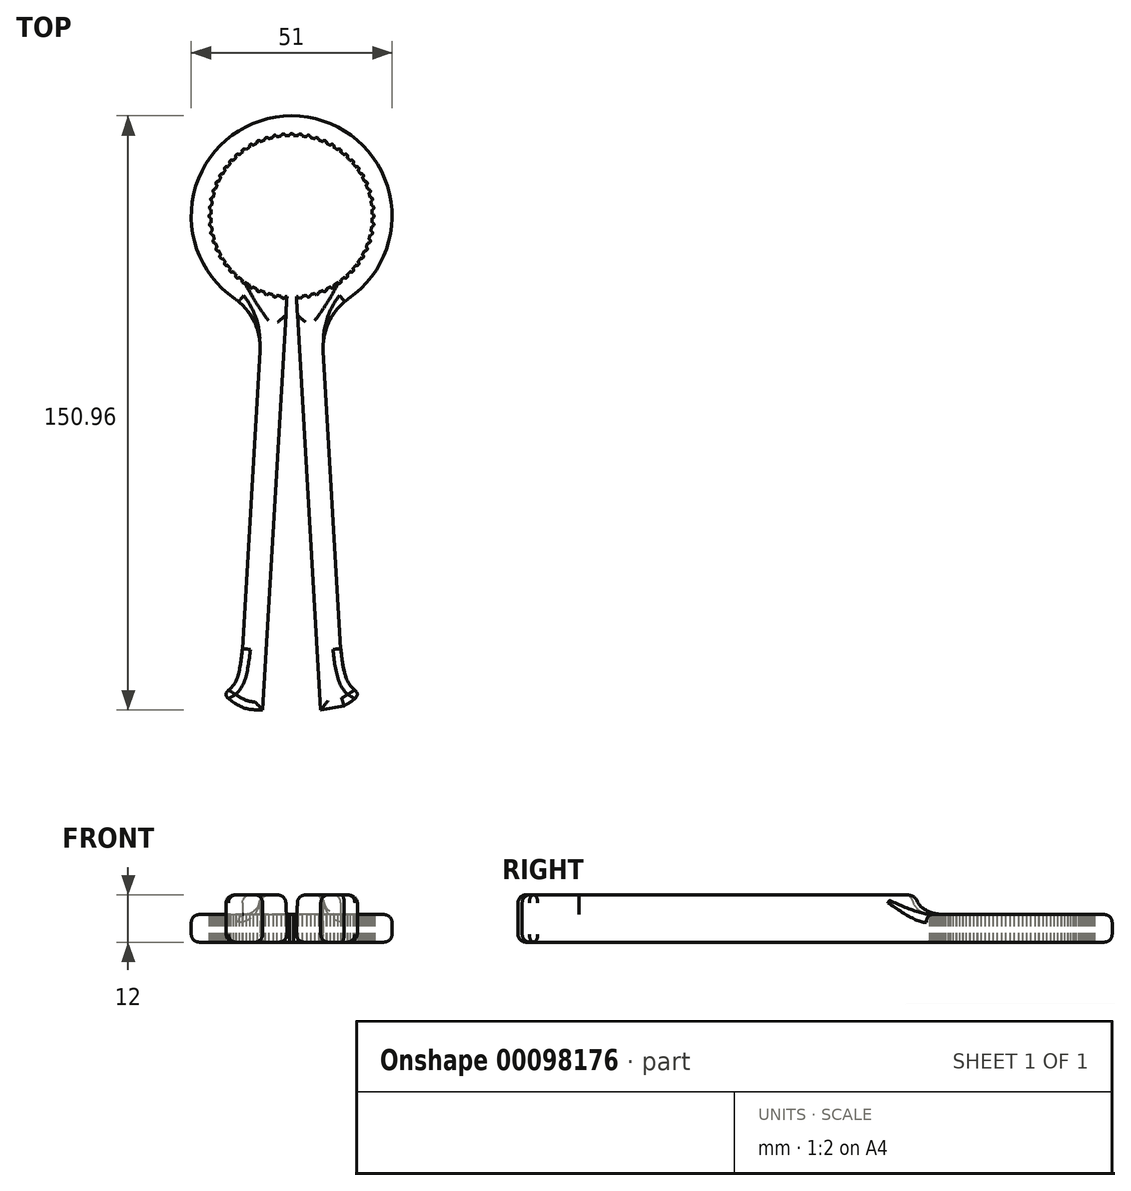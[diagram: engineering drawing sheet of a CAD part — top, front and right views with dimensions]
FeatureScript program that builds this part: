
annotation { "Feature Type Name" : "Feature", "Feature Type Description" : "" }
export const myFeature = defineFeature(function(context is Context, id is Id, definition is map)
    precondition{}
    {
        {
            var Q0;
            Q0=qCreatedBy(makeId("Top.planeOp"),FACE);
            var sketch = newSketch(context, id + "F0", { "sketchPlane" : qUnion([Q0])});
            skArc(sketch, "E0", {"start": v(-0.5, 20.5) * mm, "mid": v(0, 20) * mm, "end": v(0.5, 20.5) * mm, "construction": true});
            skArc(sketch, "E1", {"start": v(0.5, 20.5) * mm, "mid": v(0, 21) * mm, "end": v(-0.5, 20.5) * mm});
            skArc(sketch, "E2", {"start": v(-0.5, 20.5) * mm, "mid": v(-20.5, 0.35) * mm, "end": v(-1.2, -20.46) * mm});
            skArc(sketch, "E3", {"start": v(0.5, 20.5) * mm, "mid": v(0, 20.5) * mm, "end": v(-0.5, 20.5) * mm, "construction": true});
            skArc(sketch, "E4.1.0", {"start": v(-1.64, 20.43) * mm, "mid": v(-2.2, 20.88) * mm, "end": v(-2.64, 20.33) * mm});
            skArc(sketch, "E4.2.0", {"start": v(-3.77, 20.15) * mm, "mid": v(-4.37, 20.54) * mm, "end": v(-4.75, 19.94) * mm});
            skArc(sketch, "E4.3.0", {"start": v(-5.86, 19.65) * mm, "mid": v(-6.49, 19.97) * mm, "end": v(-6.8, 19.34) * mm});
            skArc(sketch, "E4.4.0", {"start": v(-7.88, 18.93) * mm, "mid": v(-8.54, 19.18) * mm, "end": v(-8.8, 18.52) * mm});
            skArc(sketch, "E4.5.0", {"start": v(-9.81, 18) * mm, "mid": v(-10.5, 18.19) * mm, "end": v(-10.68, 17.5) * mm});
            skArc(sketch, "E4.6.0", {"start": v(-11.64, 16.87) * mm, "mid": v(-12.34, 16.99) * mm, "end": v(-12.45, 16.29) * mm});
            skArc(sketch, "E4.7.0", {"start": v(-13.34, 15.56) * mm, "mid": v(-14.05, 15.6) * mm, "end": v(-14.08, 14.9) * mm});
            skArc(sketch, "E4.8.0", {"start": v(-14.9, 14.08) * mm, "mid": v(-15.6, 14.05) * mm, "end": v(-15.56, 13.34) * mm});
            skArc(sketch, "E4.9.0", {"start": v(-16.29, 12.45) * mm, "mid": v(-16.99, 12.34) * mm, "end": v(-16.87, 11.64) * mm});
            skArc(sketch, "E4.10.0", {"start": v(-17.5, 10.68) * mm, "mid": v(-18.19, 10.5) * mm, "end": v(-18, 9.81) * mm});
            skArc(sketch, "E4.11.0", {"start": v(-18.52, 8.8) * mm, "mid": v(-19.18, 8.54) * mm, "end": v(-18.93, 7.88) * mm});
            skArc(sketch, "E4.12.0", {"start": v(-19.34, 6.8) * mm, "mid": v(-19.97, 6.49) * mm, "end": v(-19.65, 5.86) * mm});
            skArc(sketch, "E4.13.0", {"start": v(-19.94, 4.75) * mm, "mid": v(-20.54, 4.37) * mm, "end": v(-20.15, 3.77) * mm});
            skArc(sketch, "E4.14.0", {"start": v(-20.33, 2.64) * mm, "mid": v(-20.88, 2.2) * mm, "end": v(-20.43, 1.64) * mm});
            skArc(sketch, "E4.15.0", {"start": v(-20.5, 0.5) * mm, "mid": v(-21, 0) * mm, "end": v(-20.5, -0.5) * mm});
            skArc(sketch, "E4.16.0", {"start": v(-20.43, -1.64) * mm, "mid": v(-20.88, -2.2) * mm, "end": v(-20.33, -2.64) * mm});
            skArc(sketch, "E4.17.0", {"start": v(-20.15, -3.77) * mm, "mid": v(-20.54, -4.37) * mm, "end": v(-19.94, -4.75) * mm});
            skArc(sketch, "E4.18.0", {"start": v(-19.65, -5.86) * mm, "mid": v(-19.97, -6.49) * mm, "end": v(-19.34, -6.8) * mm});
            skArc(sketch, "E4.19.0", {"start": v(-18.93, -7.88) * mm, "mid": v(-19.18, -8.54) * mm, "end": v(-18.52, -8.8) * mm});
            skArc(sketch, "E4.20.0", {"start": v(-18, -9.81) * mm, "mid": v(-18.19, -10.5) * mm, "end": v(-17.5, -10.68) * mm});
            skArc(sketch, "E4.21.0", {"start": v(-16.87, -11.64) * mm, "mid": v(-16.99, -12.34) * mm, "end": v(-16.29, -12.45) * mm});
            skArc(sketch, "E4.22.0", {"start": v(-15.56, -13.34) * mm, "mid": v(-15.6, -14.05) * mm, "end": v(-14.9, -14.08) * mm});
            skArc(sketch, "E4.23.0", {"start": v(-14.08, -14.9) * mm, "mid": v(-14.05, -15.6) * mm, "end": v(-13.34, -15.56) * mm});
            skArc(sketch, "E4.24.0", {"start": v(-12.45, -16.29) * mm, "mid": v(-12.34, -16.99) * mm, "end": v(-11.64, -16.87) * mm});
            skArc(sketch, "E4.25.0", {"start": v(-10.68, -17.5) * mm, "mid": v(-10.5, -18.19) * mm, "end": v(-9.81, -18) * mm});
            skArc(sketch, "E4.26.0", {"start": v(-8.8, -18.52) * mm, "mid": v(-8.54, -19.18) * mm, "end": v(-7.88, -18.93) * mm});
            skArc(sketch, "E4.27.0", {"start": v(-6.8, -19.34) * mm, "mid": v(-6.49, -19.97) * mm, "end": v(-5.86, -19.65) * mm});
            skArc(sketch, "E4.28.0", {"start": v(-4.75, -19.94) * mm, "mid": v(-4.37, -20.54) * mm, "end": v(-3.77, -20.15) * mm});
            skArc(sketch, "E4.29.0", {"start": v(-2.64, -20.33) * mm, "mid": v(-2.2, -20.88) * mm, "end": v(-1.64, -20.43) * mm});
            skArc(sketch, "E4.31.0", {"start": v(1.64, -20.43) * mm, "mid": v(2.2, -20.88) * mm, "end": v(2.64, -20.33) * mm});
            skArc(sketch, "E4.32.0", {"start": v(3.77, -20.15) * mm, "mid": v(4.37, -20.54) * mm, "end": v(4.75, -19.94) * mm});
            skArc(sketch, "E4.33.0", {"start": v(5.86, -19.65) * mm, "mid": v(6.49, -19.97) * mm, "end": v(6.8, -19.34) * mm});
            skArc(sketch, "E4.34.0", {"start": v(7.88, -18.93) * mm, "mid": v(8.54, -19.18) * mm, "end": v(8.8, -18.52) * mm});
            skArc(sketch, "E4.35.0", {"start": v(9.81, -18) * mm, "mid": v(10.5, -18.19) * mm, "end": v(10.68, -17.5) * mm});
            skArc(sketch, "E4.36.0", {"start": v(11.64, -16.87) * mm, "mid": v(12.34, -16.99) * mm, "end": v(12.45, -16.29) * mm});
            skArc(sketch, "E4.37.0", {"start": v(13.34, -15.56) * mm, "mid": v(14.05, -15.6) * mm, "end": v(14.08, -14.9) * mm});
            skArc(sketch, "E4.38.0", {"start": v(14.9, -14.08) * mm, "mid": v(15.6, -14.05) * mm, "end": v(15.56, -13.34) * mm});
            skArc(sketch, "E4.39.0", {"start": v(16.29, -12.45) * mm, "mid": v(16.99, -12.34) * mm, "end": v(16.87, -11.64) * mm});
            skArc(sketch, "E4.40.0", {"start": v(17.5, -10.68) * mm, "mid": v(18.19, -10.5) * mm, "end": v(18, -9.81) * mm});
            skArc(sketch, "E4.41.0", {"start": v(18.52, -8.8) * mm, "mid": v(19.18, -8.54) * mm, "end": v(18.93, -7.88) * mm});
            skArc(sketch, "E4.42.0", {"start": v(19.34, -6.8) * mm, "mid": v(19.97, -6.49) * mm, "end": v(19.65, -5.86) * mm});
            skArc(sketch, "E4.43.0", {"start": v(19.94, -4.75) * mm, "mid": v(20.54, -4.37) * mm, "end": v(20.15, -3.77) * mm});
            skArc(sketch, "E4.44.0", {"start": v(20.33, -2.64) * mm, "mid": v(20.88, -2.2) * mm, "end": v(20.43, -1.64) * mm});
            skArc(sketch, "E4.45.0", {"start": v(20.5, -0.5) * mm, "mid": v(21, 0) * mm, "end": v(20.5, 0.5) * mm});
            skArc(sketch, "E4.46.0", {"start": v(20.43, 1.64) * mm, "mid": v(20.88, 2.2) * mm, "end": v(20.33, 2.64) * mm});
            skArc(sketch, "E4.47.0", {"start": v(20.15, 3.77) * mm, "mid": v(20.54, 4.37) * mm, "end": v(19.94, 4.75) * mm});
            skArc(sketch, "E4.48.0", {"start": v(19.65, 5.86) * mm, "mid": v(19.97, 6.49) * mm, "end": v(19.34, 6.8) * mm});
            skArc(sketch, "E4.49.0", {"start": v(18.93, 7.88) * mm, "mid": v(19.18, 8.54) * mm, "end": v(18.52, 8.8) * mm});
            skArc(sketch, "E4.50.0", {"start": v(18, 9.81) * mm, "mid": v(18.19, 10.5) * mm, "end": v(17.5, 10.68) * mm});
            skArc(sketch, "E4.51.0", {"start": v(16.87, 11.64) * mm, "mid": v(16.99, 12.34) * mm, "end": v(16.29, 12.45) * mm});
            skArc(sketch, "E4.52.0", {"start": v(15.56, 13.34) * mm, "mid": v(15.6, 14.05) * mm, "end": v(14.9, 14.08) * mm});
            skArc(sketch, "E4.53.0", {"start": v(14.08, 14.9) * mm, "mid": v(14.05, 15.6) * mm, "end": v(13.34, 15.56) * mm});
            skArc(sketch, "E4.54.0", {"start": v(12.45, 16.29) * mm, "mid": v(12.34, 16.99) * mm, "end": v(11.64, 16.87) * mm});
            skArc(sketch, "E4.55.0", {"start": v(10.68, 17.5) * mm, "mid": v(10.5, 18.19) * mm, "end": v(9.81, 18) * mm});
            skArc(sketch, "E4.56.0", {"start": v(8.8, 18.52) * mm, "mid": v(8.54, 19.18) * mm, "end": v(7.88, 18.93) * mm});
            skArc(sketch, "E4.57.0", {"start": v(6.8, 19.34) * mm, "mid": v(6.49, 19.97) * mm, "end": v(5.86, 19.65) * mm});
            skArc(sketch, "E4.58.0", {"start": v(4.75, 19.94) * mm, "mid": v(4.37, 20.54) * mm, "end": v(3.77, 20.15) * mm});
            skArc(sketch, "E4.59.0", {"start": v(2.64, 20.33) * mm, "mid": v(2.2, 20.88) * mm, "end": v(1.64, 20.43) * mm});
            skLineSegment(sketch, "E5", {"start": v(0, 0) * mm, "end": v(0, -25.5) * mm, "construction": true});
            skLineSegment(sketch, "E6", {"start": v(0, 0) * mm, "end": v(-1.2, -20.46) * mm, "construction": true});
            skLineSegment(sketch, "E7.MirrorCS", {"start": v(0, 0) * mm, "end": v(1.2, -20.46) * mm, "construction": true});
            skLineSegment(sketch, "E8", {"start": v(-1.2, -20.46) * mm, "end": v(-7.4, -125.46) * mm});
            skArc(sketch, "E9", {"start": v(1.2, -20.46) * mm, "mid": v(20.5, 0.35) * mm, "end": v(0.5, 20.5) * mm});
            skLineSegment(sketch, "E10", {"start": v(1.2, -20.46) * mm, "end": v(1.5, -25.46) * mm});
            skArc(sketch, "E11", {"start": v(-1.5, -25.46) * mm, "mid": v(0, -25.5) * mm, "end": v(1.5, -25.46) * mm, "construction": true});
            skArc(sketch, "E12", {"start": v(1.5, -25.46) * mm, "mid": v(0, 25.5) * mm, "end": v(-1.5, -25.46) * mm});
            skPoint(sketch, "E13.orphan", {"position": v(-1.5, -25.46) * mm});
            skLineSegment(sketch, "E14", {"start": v(-7.45, -24.39) * mm, "end": v(-12.49, -109.92) * mm});
            skLineSegment(sketch, "E15.MirrorCS", {"start": v(1.2, -20.46) * mm, "end": v(7.4, -125.46) * mm});
            skLineSegment(sketch, "E16.MirrorCS", {"start": v(7.45, -24.39) * mm, "end": v(12.49, -109.92) * mm});
            skLineSegment(sketch, "E17.MirrorCS", {"start": v(13.34, -124.39) * mm, "end": v(7.4, -125.46) * mm});
            skLineSegment(sketch, "E18", {"start": v(0, 0) * mm, "end": v(0, -128.97) * mm, "construction": true});
            skFitSpline(sketch, "E19", {"points": [v(-12.49, -109.92) * mm, v(-14.7, -119.04) * mm, v(-16.69, -121.57) * mm, v(-13.34, -124.39) * mm, v(-7.4, -125.46) * mm], "startDerivative": vector(-3.66, -30.82) * mm, "endDerivative": vector(39.2, 0) * mm});
            skLineSegment(sketch, "E20", {"start": v(-12.49, -109.92) * mm, "end": v(-13.34, -124.39) * mm, "construction": true});
            skFitSpline(sketch, "E21.MirrorCS", {"points": [v(12.49, -109.92) * mm, v(14.7, -119.04) * mm, v(16.69, -121.57) * mm, v(13.34, -124.39) * mm, v(7.4, -125.46) * mm], "startDerivative": vector(3.66, -30.82) * mm, "endDerivative": vector(-39.2, 0) * mm});
            skLineSegment(sketch, "E22", {"start": v(12.49, -109.92) * mm, "end": v(13.34, -124.39) * mm, "construction": true});
            skSolve(sketch);
        }
        {
            var Q0;
            {var subQ63=sQuery(id+"F0.wireOp",EDGE,"E1");Q0=makeQuery(id+"F0.imprint","IMPRINT",FACE,{"disambiguationData":[TD([[makeQuery(id+"F0.imprint","IMPRINT",EDGE,{"derivedFrom":subQ63}),-1.0]])]});}
            var Q1;
            {var subQ4=sQuery(id+"F0.wireOp",EDGE,"E14");Q1=makeQuery(id+"F0.imprint","IMPRINT",FACE,{"disambiguationData":[TD([[makeQuery(id+"F0.imprint","IMPRINT",EDGE,{"derivedFrom":subQ4}),1.0]])]});}
            var Q2;
            {var subQ3=sQuery(id+"F0.wireOp",EDGE,"E16.MirrorCS");Q2=makeQuery(id+"F0.imprint","IMPRINT",FACE,{"disambiguationData":[TD([[makeQuery(id+"F0.imprint","IMPRINT",EDGE,{"derivedFrom":subQ3}),-1.0]])]});}
            extrude(context, id + "F1", {"entities" : qUnion([Q0, Q1, Q2]), "depth" : 7 * mm});
        }
        {
            var Q0;
            Q0=makeQuery(id+"F1.opExtrude","SWEPT_EDGE",EDGE,{"disambiguationData":[OSD([sQuery(id+"F0.wireOp",EDGE,"E12"),sQuery(id+"F0.wireOp",EDGE,"E14")])]});
            var Q1;
            Q1=makeQuery(id+"F1.opExtrude","SWEPT_EDGE",EDGE,{"disambiguationData":[OSD([sQuery(id+"F0.wireOp",EDGE,"E12"),sQuery(id+"F0.wireOp",EDGE,"E16.MirrorCS")])]});
            fillet(context, id + "F2", {"entities" : qUnion([Q0, Q1]), "radius" : 15 * mm, "tangentPropagation" : true, "allowEdgeOverflow" : false});
        }
        {
            var Q0;
            Q0=makeQuery(id+"F1.opExtrude","SWEPT_EDGE",EDGE,{"disambiguationData":[OSD([sQuery(id+"F0.wireOp",EDGE,"E14"),sQuery(id+"F0.wireOp",EDGE,"XZCalI78-Oa4T-IdOj-XRzA-xECI0NogZIKb")])]});
            var Q1;
            Q1=makeQuery(id+"F1.opExtrude","SWEPT_EDGE",EDGE,{"disambiguationData":[OSD([sQuery(id+"F0.wireOp",EDGE,"E16.MirrorCS"),sQuery(id+"F0.wireOp",EDGE,"E17.MirrorCS")])]});
            fillet(context, id + "F3", {"entities" : qUnion([Q0, Q1]), "radius" : 5 * mm, "tangentPropagation" : true, "allowEdgeOverflow" : false});
        }
        {
            var Q0;
            {var subQ4=sQuery(id+"F0.wireOp",EDGE,"E14");Q0=makeQuery(id+"F0.imprint","IMPRINT",FACE,{"disambiguationData":[TD([[makeQuery(id+"F0.imprint","IMPRINT",EDGE,{"derivedFrom":subQ4}),1.0]])]});}
            var Q1;
            {var subQ3=sQuery(id+"F0.wireOp",EDGE,"E16.MirrorCS");Q1=makeQuery(id+"F0.imprint","IMPRINT",FACE,{"disambiguationData":[TD([[makeQuery(id+"F0.imprint","IMPRINT",EDGE,{"derivedFrom":subQ3}),-1.0]])]});}
            extrude(context, id + "F4", {"entities" : qUnion([Q0, Q1]), "operationType" : NewBodyOperationType.ADD, "depth" : 12 * mm});
        }
        {
            var Q0;
            {var subQ0=sQuery(id+"F0.wireOp",EDGE,"E14");Q0=makeQuery(id+"F4.boolean.opBoolean","INTERSECT",EDGE,{"derivedFrom":[makeQuery(id+"F1.opExtrude","CAP_FACE",FACE,{"disambiguationData":[OSD([sQuery(id+"F0.wireOp",EDGE,"E1"),sQuery(id+"F0.wireOp",EDGE,"E2"),sQuery(id+"F0.wireOp",EDGE,"E4.1.0"),sQuery(id+"F0.wireOp",EDGE,"E4.2.0"),sQuery(id+"F0.wireOp",EDGE,"E4.3.0"),sQuery(id+"F0.wireOp",EDGE,"E4.4.0"),sQuery(id+"F0.wireOp",EDGE,"E4.5.0"),sQuery(id+"F0.wireOp",EDGE,"E4.6.0"),sQuery(id+"F0.wireOp",EDGE,"E4.7.0"),sQuery(id+"F0.wireOp",EDGE,"E4.8.0"),sQuery(id+"F0.wireOp",EDGE,"E4.9.0"),sQuery(id+"F0.wireOp",EDGE,"E4.10.0"),sQuery(id+"F0.wireOp",EDGE,"E4.11.0"),sQuery(id+"F0.wireOp",EDGE,"E4.12.0"),sQuery(id+"F0.wireOp",EDGE,"E4.13.0"),sQuery(id+"F0.wireOp",EDGE,"E4.14.0"),sQuery(id+"F0.wireOp",EDGE,"E4.15.0"),sQuery(id+"F0.wireOp",EDGE,"E4.16.0"),sQuery(id+"F0.wireOp",EDGE,"E4.17.0"),sQuery(id+"F0.wireOp",EDGE,"E4.18.0"),sQuery(id+"F0.wireOp",EDGE,"E4.19.0"),sQuery(id+"F0.wireOp",EDGE,"E4.20.0"),sQuery(id+"F0.wireOp",EDGE,"E4.21.0"),sQuery(id+"F0.wireOp",EDGE,"E4.22.0"),sQuery(id+"F0.wireOp",EDGE,"E4.23.0"),sQuery(id+"F0.wireOp",EDGE,"E4.24.0"),sQuery(id+"F0.wireOp",EDGE,"E4.25.0"),sQuery(id+"F0.wireOp",EDGE,"E4.26.0"),sQuery(id+"F0.wireOp",EDGE,"E4.27.0"),sQuery(id+"F0.wireOp",EDGE,"E4.28.0"),sQuery(id+"F0.wireOp",EDGE,"E4.29.0"),sQuery(id+"F0.wireOp",EDGE,"E4.31.0"),sQuery(id+"F0.wireOp",EDGE,"E4.32.0"),sQuery(id+"F0.wireOp",EDGE,"E4.33.0"),sQuery(id+"F0.wireOp",EDGE,"E4.34.0"),sQuery(id+"F0.wireOp",EDGE,"E4.35.0"),sQuery(id+"F0.wireOp",EDGE,"E4.36.0"),sQuery(id+"F0.wireOp",EDGE,"E4.37.0"),sQuery(id+"F0.wireOp",EDGE,"E4.38.0"),sQuery(id+"F0.wireOp",EDGE,"E4.39.0"),sQuery(id+"F0.wireOp",EDGE,"E4.40.0"),sQuery(id+"F0.wireOp",EDGE,"E4.41.0"),sQuery(id+"F0.wireOp",EDGE,"E4.42.0"),sQuery(id+"F0.wireOp",EDGE,"E4.43.0"),sQuery(id+"F0.wireOp",EDGE,"E4.44.0"),sQuery(id+"F0.wireOp",EDGE,"E4.45.0"),sQuery(id+"F0.wireOp",EDGE,"E4.46.0"),sQuery(id+"F0.wireOp",EDGE,"E4.47.0"),sQuery(id+"F0.wireOp",EDGE,"E4.48.0"),sQuery(id+"F0.wireOp",EDGE,"E4.49.0"),sQuery(id+"F0.wireOp",EDGE,"E4.50.0"),sQuery(id+"F0.wireOp",EDGE,"E4.51.0"),sQuery(id+"F0.wireOp",EDGE,"E4.52.0"),sQuery(id+"F0.wireOp",EDGE,"E4.53.0"),sQuery(id+"F0.wireOp",EDGE,"E4.54.0"),sQuery(id+"F0.wireOp",EDGE,"E4.55.0"),sQuery(id+"F0.wireOp",EDGE,"E4.56.0"),sQuery(id+"F0.wireOp",EDGE,"E4.57.0"),sQuery(id+"F0.wireOp",EDGE,"E4.58.0"),sQuery(id+"F0.wireOp",EDGE,"E4.59.0"),sQuery(id+"F0.wireOp",EDGE,"E8"),sQuery(id+"F0.wireOp",EDGE,"E9"),sQuery(id+"F0.wireOp",EDGE,"E12"),subQ0,sQuery(id+"F0.wireOp",EDGE,"E15.MirrorCS"),sQuery(id+"F0.wireOp",EDGE,"E16.MirrorCS"),sQuery(id+"F0.wireOp",EDGE,"E17.MirrorCS"),sQuery(id+"F0.wireOp",EDGE,"E19"),sQuery(id+"F0.wireOp",EDGE,"E21.MirrorCS")])],"isStart":false}),makeQuery(id+"F4.opExtrude","SWEPT_FACE",FACE,{"disambiguationData":[OSD([subQ0])]})]});}
            fillet(context, id + "F5", {"entities" : qUnion([Q0]), "radius" : 5 * mm, "tangentPropagation" : true, "allowEdgeOverflow" : false});
        }
        {
            var Q0;
            {var subQ0=sQuery(id+"F0.wireOp",EDGE,"E16.MirrorCS");Q0=makeQuery(id+"F4.boolean.opBoolean","INTERSECT",EDGE,{"derivedFrom":[makeQuery(id+"F1.opExtrude","CAP_FACE",FACE,{"disambiguationData":[OSD([sQuery(id+"F0.wireOp",EDGE,"E1"),sQuery(id+"F0.wireOp",EDGE,"E2"),sQuery(id+"F0.wireOp",EDGE,"E4.1.0"),sQuery(id+"F0.wireOp",EDGE,"E4.2.0"),sQuery(id+"F0.wireOp",EDGE,"E4.3.0"),sQuery(id+"F0.wireOp",EDGE,"E4.4.0"),sQuery(id+"F0.wireOp",EDGE,"E4.5.0"),sQuery(id+"F0.wireOp",EDGE,"E4.6.0"),sQuery(id+"F0.wireOp",EDGE,"E4.7.0"),sQuery(id+"F0.wireOp",EDGE,"E4.8.0"),sQuery(id+"F0.wireOp",EDGE,"E4.9.0"),sQuery(id+"F0.wireOp",EDGE,"E4.10.0"),sQuery(id+"F0.wireOp",EDGE,"E4.11.0"),sQuery(id+"F0.wireOp",EDGE,"E4.12.0"),sQuery(id+"F0.wireOp",EDGE,"E4.13.0"),sQuery(id+"F0.wireOp",EDGE,"E4.14.0"),sQuery(id+"F0.wireOp",EDGE,"E4.15.0"),sQuery(id+"F0.wireOp",EDGE,"E4.16.0"),sQuery(id+"F0.wireOp",EDGE,"E4.17.0"),sQuery(id+"F0.wireOp",EDGE,"E4.18.0"),sQuery(id+"F0.wireOp",EDGE,"E4.19.0"),sQuery(id+"F0.wireOp",EDGE,"E4.20.0"),sQuery(id+"F0.wireOp",EDGE,"E4.21.0"),sQuery(id+"F0.wireOp",EDGE,"E4.22.0"),sQuery(id+"F0.wireOp",EDGE,"E4.23.0"),sQuery(id+"F0.wireOp",EDGE,"E4.24.0"),sQuery(id+"F0.wireOp",EDGE,"E4.25.0"),sQuery(id+"F0.wireOp",EDGE,"E4.26.0"),sQuery(id+"F0.wireOp",EDGE,"E4.27.0"),sQuery(id+"F0.wireOp",EDGE,"E4.28.0"),sQuery(id+"F0.wireOp",EDGE,"E4.29.0"),sQuery(id+"F0.wireOp",EDGE,"E4.31.0"),sQuery(id+"F0.wireOp",EDGE,"E4.32.0"),sQuery(id+"F0.wireOp",EDGE,"E4.33.0"),sQuery(id+"F0.wireOp",EDGE,"E4.34.0"),sQuery(id+"F0.wireOp",EDGE,"E4.35.0"),sQuery(id+"F0.wireOp",EDGE,"E4.36.0"),sQuery(id+"F0.wireOp",EDGE,"E4.37.0"),sQuery(id+"F0.wireOp",EDGE,"E4.38.0"),sQuery(id+"F0.wireOp",EDGE,"E4.39.0"),sQuery(id+"F0.wireOp",EDGE,"E4.40.0"),sQuery(id+"F0.wireOp",EDGE,"E4.41.0"),sQuery(id+"F0.wireOp",EDGE,"E4.42.0"),sQuery(id+"F0.wireOp",EDGE,"E4.43.0"),sQuery(id+"F0.wireOp",EDGE,"E4.44.0"),sQuery(id+"F0.wireOp",EDGE,"E4.45.0"),sQuery(id+"F0.wireOp",EDGE,"E4.46.0"),sQuery(id+"F0.wireOp",EDGE,"E4.47.0"),sQuery(id+"F0.wireOp",EDGE,"E4.48.0"),sQuery(id+"F0.wireOp",EDGE,"E4.49.0"),sQuery(id+"F0.wireOp",EDGE,"E4.50.0"),sQuery(id+"F0.wireOp",EDGE,"E4.51.0"),sQuery(id+"F0.wireOp",EDGE,"E4.52.0"),sQuery(id+"F0.wireOp",EDGE,"E4.53.0"),sQuery(id+"F0.wireOp",EDGE,"E4.54.0"),sQuery(id+"F0.wireOp",EDGE,"E4.55.0"),sQuery(id+"F0.wireOp",EDGE,"E4.56.0"),sQuery(id+"F0.wireOp",EDGE,"E4.57.0"),sQuery(id+"F0.wireOp",EDGE,"E4.58.0"),sQuery(id+"F0.wireOp",EDGE,"E4.59.0"),sQuery(id+"F0.wireOp",EDGE,"E8"),sQuery(id+"F0.wireOp",EDGE,"E9"),sQuery(id+"F0.wireOp",EDGE,"E12"),sQuery(id+"F0.wireOp",EDGE,"E14"),sQuery(id+"F0.wireOp",EDGE,"E15.MirrorCS"),subQ0,sQuery(id+"F0.wireOp",EDGE,"E17.MirrorCS"),sQuery(id+"F0.wireOp",EDGE,"E19"),sQuery(id+"F0.wireOp",EDGE,"E21.MirrorCS")])],"isStart":false}),makeQuery(id+"F4.opExtrude","SWEPT_FACE",FACE,{"disambiguationData":[OSD([subQ0])]})]});}
            fillet(context, id + "F6", {"entities" : qUnion([Q0]), "radius" : 5 * mm, "tangentPropagation" : true, "allowEdgeOverflow" : false});
        }
        {
            var Q0;
            {var subQ0=sQuery(id+"F0.wireOp",EDGE,"E15.MirrorCS");var subQ1=sQuery(id+"F0.wireOp",EDGE,"E12");var subQ2=sQuery(id+"F0.wireOp",EDGE,"E16.MirrorCS");Q0=makeQuery(id+"F4.boolean.opBoolean","INTERSECT",EDGE,{"derivedFrom":[makeQuery(id+"F1.opExtrude","CAP_FACE",FACE,{"disambiguationData":[OSD([sQuery(id+"F0.wireOp",EDGE,"E1"),sQuery(id+"F0.wireOp",EDGE,"E2"),sQuery(id+"F0.wireOp",EDGE,"E4.1.0"),sQuery(id+"F0.wireOp",EDGE,"E4.2.0"),sQuery(id+"F0.wireOp",EDGE,"E4.3.0"),sQuery(id+"F0.wireOp",EDGE,"E4.4.0"),sQuery(id+"F0.wireOp",EDGE,"E4.5.0"),sQuery(id+"F0.wireOp",EDGE,"E4.6.0"),sQuery(id+"F0.wireOp",EDGE,"E4.7.0"),sQuery(id+"F0.wireOp",EDGE,"E4.8.0"),sQuery(id+"F0.wireOp",EDGE,"E4.9.0"),sQuery(id+"F0.wireOp",EDGE,"E4.10.0"),sQuery(id+"F0.wireOp",EDGE,"E4.11.0"),sQuery(id+"F0.wireOp",EDGE,"E4.12.0"),sQuery(id+"F0.wireOp",EDGE,"E4.13.0"),sQuery(id+"F0.wireOp",EDGE,"E4.14.0"),sQuery(id+"F0.wireOp",EDGE,"E4.15.0"),sQuery(id+"F0.wireOp",EDGE,"E4.16.0"),sQuery(id+"F0.wireOp",EDGE,"E4.17.0"),sQuery(id+"F0.wireOp",EDGE,"E4.18.0"),sQuery(id+"F0.wireOp",EDGE,"E4.19.0"),sQuery(id+"F0.wireOp",EDGE,"E4.20.0"),sQuery(id+"F0.wireOp",EDGE,"E4.21.0"),sQuery(id+"F0.wireOp",EDGE,"E4.22.0"),sQuery(id+"F0.wireOp",EDGE,"E4.23.0"),sQuery(id+"F0.wireOp",EDGE,"E4.24.0"),sQuery(id+"F0.wireOp",EDGE,"E4.25.0"),sQuery(id+"F0.wireOp",EDGE,"E4.26.0"),sQuery(id+"F0.wireOp",EDGE,"E4.27.0"),sQuery(id+"F0.wireOp",EDGE,"E4.28.0"),sQuery(id+"F0.wireOp",EDGE,"E4.29.0"),sQuery(id+"F0.wireOp",EDGE,"E4.31.0"),sQuery(id+"F0.wireOp",EDGE,"E4.32.0"),sQuery(id+"F0.wireOp",EDGE,"E4.33.0"),sQuery(id+"F0.wireOp",EDGE,"E4.34.0"),sQuery(id+"F0.wireOp",EDGE,"E4.35.0"),sQuery(id+"F0.wireOp",EDGE,"E4.36.0"),sQuery(id+"F0.wireOp",EDGE,"E4.37.0"),sQuery(id+"F0.wireOp",EDGE,"E4.38.0"),sQuery(id+"F0.wireOp",EDGE,"E4.39.0"),sQuery(id+"F0.wireOp",EDGE,"E4.40.0"),sQuery(id+"F0.wireOp",EDGE,"E4.41.0"),sQuery(id+"F0.wireOp",EDGE,"E4.42.0"),sQuery(id+"F0.wireOp",EDGE,"E4.43.0"),sQuery(id+"F0.wireOp",EDGE,"E4.44.0"),sQuery(id+"F0.wireOp",EDGE,"E4.45.0"),sQuery(id+"F0.wireOp",EDGE,"E4.46.0"),sQuery(id+"F0.wireOp",EDGE,"E4.47.0"),sQuery(id+"F0.wireOp",EDGE,"E4.48.0"),sQuery(id+"F0.wireOp",EDGE,"E4.49.0"),sQuery(id+"F0.wireOp",EDGE,"E4.50.0"),sQuery(id+"F0.wireOp",EDGE,"E4.51.0"),sQuery(id+"F0.wireOp",EDGE,"E4.52.0"),sQuery(id+"F0.wireOp",EDGE,"E4.53.0"),sQuery(id+"F0.wireOp",EDGE,"E4.54.0"),sQuery(id+"F0.wireOp",EDGE,"E4.55.0"),sQuery(id+"F0.wireOp",EDGE,"E4.56.0"),sQuery(id+"F0.wireOp",EDGE,"E4.57.0"),sQuery(id+"F0.wireOp",EDGE,"E4.58.0"),sQuery(id+"F0.wireOp",EDGE,"E4.59.0"),sQuery(id+"F0.wireOp",EDGE,"E8"),sQuery(id+"F0.wireOp",EDGE,"E9"),subQ1,sQuery(id+"F0.wireOp",EDGE,"E14"),subQ0,subQ2,sQuery(id+"F0.wireOp",EDGE,"E17.MirrorCS"),sQuery(id+"F0.wireOp",EDGE,"E19"),sQuery(id+"F0.wireOp",EDGE,"E21.MirrorCS")])],"isStart":false}),makeQuery(id+"F4.opExtrude","SWEPT_FACE",FACE,{"disambiguationData":[OSD([subQ1]),TDD([makeQuery(id+"F0.imprint","IMPRINT",EDGE,{"disambiguationData":[TD([[makeQuery(id+"F0.imprint","INTERSECT",VERTEX,{"derivedFrom":[subQ1,subQ0]}),-1.0]])],"derivedFrom":subQ1})])]})]});}
            var Q1;
            {var subQ0=sQuery(id+"F0.wireOp",EDGE,"E12");var subQ1=sQuery(id+"F0.wireOp",EDGE,"E8");var subQ2=sQuery(id+"F0.wireOp",EDGE,"E14");Q1=makeQuery(id+"F4.boolean.opBoolean","INTERSECT",EDGE,{"derivedFrom":[makeQuery(id+"F1.opExtrude","CAP_FACE",FACE,{"disambiguationData":[OSD([sQuery(id+"F0.wireOp",EDGE,"E1"),sQuery(id+"F0.wireOp",EDGE,"E2"),sQuery(id+"F0.wireOp",EDGE,"E4.1.0"),sQuery(id+"F0.wireOp",EDGE,"E4.2.0"),sQuery(id+"F0.wireOp",EDGE,"E4.3.0"),sQuery(id+"F0.wireOp",EDGE,"E4.4.0"),sQuery(id+"F0.wireOp",EDGE,"E4.5.0"),sQuery(id+"F0.wireOp",EDGE,"E4.6.0"),sQuery(id+"F0.wireOp",EDGE,"E4.7.0"),sQuery(id+"F0.wireOp",EDGE,"E4.8.0"),sQuery(id+"F0.wireOp",EDGE,"E4.9.0"),sQuery(id+"F0.wireOp",EDGE,"E4.10.0"),sQuery(id+"F0.wireOp",EDGE,"E4.11.0"),sQuery(id+"F0.wireOp",EDGE,"E4.12.0"),sQuery(id+"F0.wireOp",EDGE,"E4.13.0"),sQuery(id+"F0.wireOp",EDGE,"E4.14.0"),sQuery(id+"F0.wireOp",EDGE,"E4.15.0"),sQuery(id+"F0.wireOp",EDGE,"E4.16.0"),sQuery(id+"F0.wireOp",EDGE,"E4.17.0"),sQuery(id+"F0.wireOp",EDGE,"E4.18.0"),sQuery(id+"F0.wireOp",EDGE,"E4.19.0"),sQuery(id+"F0.wireOp",EDGE,"E4.20.0"),sQuery(id+"F0.wireOp",EDGE,"E4.21.0"),sQuery(id+"F0.wireOp",EDGE,"E4.22.0"),sQuery(id+"F0.wireOp",EDGE,"E4.23.0"),sQuery(id+"F0.wireOp",EDGE,"E4.24.0"),sQuery(id+"F0.wireOp",EDGE,"E4.25.0"),sQuery(id+"F0.wireOp",EDGE,"E4.26.0"),sQuery(id+"F0.wireOp",EDGE,"E4.27.0"),sQuery(id+"F0.wireOp",EDGE,"E4.28.0"),sQuery(id+"F0.wireOp",EDGE,"E4.29.0"),sQuery(id+"F0.wireOp",EDGE,"E4.31.0"),sQuery(id+"F0.wireOp",EDGE,"E4.32.0"),sQuery(id+"F0.wireOp",EDGE,"E4.33.0"),sQuery(id+"F0.wireOp",EDGE,"E4.34.0"),sQuery(id+"F0.wireOp",EDGE,"E4.35.0"),sQuery(id+"F0.wireOp",EDGE,"E4.36.0"),sQuery(id+"F0.wireOp",EDGE,"E4.37.0"),sQuery(id+"F0.wireOp",EDGE,"E4.38.0"),sQuery(id+"F0.wireOp",EDGE,"E4.39.0"),sQuery(id+"F0.wireOp",EDGE,"E4.40.0"),sQuery(id+"F0.wireOp",EDGE,"E4.41.0"),sQuery(id+"F0.wireOp",EDGE,"E4.42.0"),sQuery(id+"F0.wireOp",EDGE,"E4.43.0"),sQuery(id+"F0.wireOp",EDGE,"E4.44.0"),sQuery(id+"F0.wireOp",EDGE,"E4.45.0"),sQuery(id+"F0.wireOp",EDGE,"E4.46.0"),sQuery(id+"F0.wireOp",EDGE,"E4.47.0"),sQuery(id+"F0.wireOp",EDGE,"E4.48.0"),sQuery(id+"F0.wireOp",EDGE,"E4.49.0"),sQuery(id+"F0.wireOp",EDGE,"E4.50.0"),sQuery(id+"F0.wireOp",EDGE,"E4.51.0"),sQuery(id+"F0.wireOp",EDGE,"E4.52.0"),sQuery(id+"F0.wireOp",EDGE,"E4.53.0"),sQuery(id+"F0.wireOp",EDGE,"E4.54.0"),sQuery(id+"F0.wireOp",EDGE,"E4.55.0"),sQuery(id+"F0.wireOp",EDGE,"E4.56.0"),sQuery(id+"F0.wireOp",EDGE,"E4.57.0"),sQuery(id+"F0.wireOp",EDGE,"E4.58.0"),sQuery(id+"F0.wireOp",EDGE,"E4.59.0"),subQ1,sQuery(id+"F0.wireOp",EDGE,"E9"),subQ0,subQ2,sQuery(id+"F0.wireOp",EDGE,"E15.MirrorCS"),sQuery(id+"F0.wireOp",EDGE,"E16.MirrorCS"),sQuery(id+"F0.wireOp",EDGE,"E17.MirrorCS"),sQuery(id+"F0.wireOp",EDGE,"E19"),sQuery(id+"F0.wireOp",EDGE,"E21.MirrorCS")])],"isStart":false}),makeQuery(id+"F4.opExtrude","SWEPT_FACE",FACE,{"disambiguationData":[OSD([subQ0]),TDD([makeQuery(id+"F0.imprint","IMPRINT",EDGE,{"disambiguationData":[TD([[makeQuery(id+"F0.imprint","INTERSECT",VERTEX,{"derivedFrom":[subQ1,subQ0]}),1.0]])],"derivedFrom":subQ0})])]})]});}
            fillet(context, id + "F7", {"entities" : qUnion([Q0, Q1]), "radius" : 5 * mm, "tangentPropagation" : true, "allowEdgeOverflow" : false});
        }
        {
            var Q0;
            Q0=makeQuery(id+"F4.opExtrude","CAP_EDGE",EDGE,{"disambiguationData":[OSD([sQuery(id+"F0.wireOp",EDGE,"E14")])],"isStart":false});
            var Q1;
            {var subQ0=sQuery(id+"F0.wireOp",EDGE,"E19");var subQ1=sQuery(id+"F0.wireOp",EDGE,"E14");var subQ2=sQuery(id+"F0.wireOp",EDGE,"E12");var subQ3=sQuery(id+"F0.wireOp",EDGE,"E8");Q1=makeQuery(id+"F7.opFillet","BLEND_EDGE",EDGE,{"blendedFrom":[makeQuery(id+"F4.boolean.opBoolean","INTERSECT",EDGE,{"derivedFrom":[makeQuery(id+"F1.opExtrude","CAP_FACE",FACE,{"disambiguationData":[OSD([sQuery(id+"F0.wireOp",EDGE,"E1"),sQuery(id+"F0.wireOp",EDGE,"E2"),sQuery(id+"F0.wireOp",EDGE,"E4.1.0"),sQuery(id+"F0.wireOp",EDGE,"E4.2.0"),sQuery(id+"F0.wireOp",EDGE,"E4.3.0"),sQuery(id+"F0.wireOp",EDGE,"E4.4.0"),sQuery(id+"F0.wireOp",EDGE,"E4.5.0"),sQuery(id+"F0.wireOp",EDGE,"E4.6.0"),sQuery(id+"F0.wireOp",EDGE,"E4.7.0"),sQuery(id+"F0.wireOp",EDGE,"E4.8.0"),sQuery(id+"F0.wireOp",EDGE,"E4.9.0"),sQuery(id+"F0.wireOp",EDGE,"E4.10.0"),sQuery(id+"F0.wireOp",EDGE,"E4.11.0"),sQuery(id+"F0.wireOp",EDGE,"E4.12.0"),sQuery(id+"F0.wireOp",EDGE,"E4.13.0"),sQuery(id+"F0.wireOp",EDGE,"E4.14.0"),sQuery(id+"F0.wireOp",EDGE,"E4.15.0"),sQuery(id+"F0.wireOp",EDGE,"E4.16.0"),sQuery(id+"F0.wireOp",EDGE,"E4.17.0"),sQuery(id+"F0.wireOp",EDGE,"E4.18.0"),sQuery(id+"F0.wireOp",EDGE,"E4.19.0"),sQuery(id+"F0.wireOp",EDGE,"E4.20.0"),sQuery(id+"F0.wireOp",EDGE,"E4.21.0"),sQuery(id+"F0.wireOp",EDGE,"E4.22.0"),sQuery(id+"F0.wireOp",EDGE,"E4.23.0"),sQuery(id+"F0.wireOp",EDGE,"E4.24.0"),sQuery(id+"F0.wireOp",EDGE,"E4.25.0"),sQuery(id+"F0.wireOp",EDGE,"E4.26.0"),sQuery(id+"F0.wireOp",EDGE,"E4.27.0"),sQuery(id+"F0.wireOp",EDGE,"E4.28.0"),sQuery(id+"F0.wireOp",EDGE,"E4.29.0"),sQuery(id+"F0.wireOp",EDGE,"E4.31.0"),sQuery(id+"F0.wireOp",EDGE,"E4.32.0"),sQuery(id+"F0.wireOp",EDGE,"E4.33.0"),sQuery(id+"F0.wireOp",EDGE,"E4.34.0"),sQuery(id+"F0.wireOp",EDGE,"E4.35.0"),sQuery(id+"F0.wireOp",EDGE,"E4.36.0"),sQuery(id+"F0.wireOp",EDGE,"E4.37.0"),sQuery(id+"F0.wireOp",EDGE,"E4.38.0"),sQuery(id+"F0.wireOp",EDGE,"E4.39.0"),sQuery(id+"F0.wireOp",EDGE,"E4.40.0"),sQuery(id+"F0.wireOp",EDGE,"E4.41.0"),sQuery(id+"F0.wireOp",EDGE,"E4.42.0"),sQuery(id+"F0.wireOp",EDGE,"E4.43.0"),sQuery(id+"F0.wireOp",EDGE,"E4.44.0"),sQuery(id+"F0.wireOp",EDGE,"E4.45.0"),sQuery(id+"F0.wireOp",EDGE,"E4.46.0"),sQuery(id+"F0.wireOp",EDGE,"E4.47.0"),sQuery(id+"F0.wireOp",EDGE,"E4.48.0"),sQuery(id+"F0.wireOp",EDGE,"E4.49.0"),sQuery(id+"F0.wireOp",EDGE,"E4.50.0"),sQuery(id+"F0.wireOp",EDGE,"E4.51.0"),sQuery(id+"F0.wireOp",EDGE,"E4.52.0"),sQuery(id+"F0.wireOp",EDGE,"E4.53.0"),sQuery(id+"F0.wireOp",EDGE,"E4.54.0"),sQuery(id+"F0.wireOp",EDGE,"E4.55.0"),sQuery(id+"F0.wireOp",EDGE,"E4.56.0"),sQuery(id+"F0.wireOp",EDGE,"E4.57.0"),sQuery(id+"F0.wireOp",EDGE,"E4.58.0"),sQuery(id+"F0.wireOp",EDGE,"E4.59.0"),subQ3,sQuery(id+"F0.wireOp",EDGE,"E9"),subQ2,subQ1,sQuery(id+"F0.wireOp",EDGE,"E15.MirrorCS"),sQuery(id+"F0.wireOp",EDGE,"E16.MirrorCS"),sQuery(id+"F0.wireOp",EDGE,"E17.MirrorCS"),subQ0,sQuery(id+"F0.wireOp",EDGE,"E21.MirrorCS")])],"isStart":false}),makeQuery(id+"F4.opExtrude","SWEPT_FACE",FACE,{"disambiguationData":[OSD([subQ2]),TDD([makeQuery(id+"F0.imprint","IMPRINT",EDGE,{"disambiguationData":[TD([[makeQuery(id+"F0.imprint","INTERSECT",VERTEX,{"derivedFrom":[subQ3,subQ2]}),1.0]])],"derivedFrom":subQ2})])]})]}),makeQuery(id+"F4.opExtrude","CAP_FACE",FACE,{"disambiguationData":[OSD([subQ3,subQ2,subQ1,subQ0])],"isStart":false})],"blendedInto":[makeQuery(id+"F4.opExtrude","CAP_FACE",FACE,{"disambiguationData":[OSD([subQ3,subQ2,subQ1,subQ0])],"isStart":false})]});}
            var Q2;
            {var subQ0=sQuery(id+"F0.wireOp",EDGE,"E19");var subQ1=sQuery(id+"F0.wireOp",EDGE,"E14");var subQ2=sQuery(id+"F0.wireOp",EDGE,"E12");var subQ3=sQuery(id+"F0.wireOp",EDGE,"E8");Q2=makeQuery(id+"F5.opFillet","BLEND_EDGE",EDGE,{"blendedFrom":[makeQuery(id+"F4.boolean.opBoolean","INTERSECT",EDGE,{"derivedFrom":[makeQuery(id+"F1.opExtrude","CAP_FACE",FACE,{"disambiguationData":[OSD([sQuery(id+"F0.wireOp",EDGE,"E1"),sQuery(id+"F0.wireOp",EDGE,"E2"),sQuery(id+"F0.wireOp",EDGE,"E4.1.0"),sQuery(id+"F0.wireOp",EDGE,"E4.2.0"),sQuery(id+"F0.wireOp",EDGE,"E4.3.0"),sQuery(id+"F0.wireOp",EDGE,"E4.4.0"),sQuery(id+"F0.wireOp",EDGE,"E4.5.0"),sQuery(id+"F0.wireOp",EDGE,"E4.6.0"),sQuery(id+"F0.wireOp",EDGE,"E4.7.0"),sQuery(id+"F0.wireOp",EDGE,"E4.8.0"),sQuery(id+"F0.wireOp",EDGE,"E4.9.0"),sQuery(id+"F0.wireOp",EDGE,"E4.10.0"),sQuery(id+"F0.wireOp",EDGE,"E4.11.0"),sQuery(id+"F0.wireOp",EDGE,"E4.12.0"),sQuery(id+"F0.wireOp",EDGE,"E4.13.0"),sQuery(id+"F0.wireOp",EDGE,"E4.14.0"),sQuery(id+"F0.wireOp",EDGE,"E4.15.0"),sQuery(id+"F0.wireOp",EDGE,"E4.16.0"),sQuery(id+"F0.wireOp",EDGE,"E4.17.0"),sQuery(id+"F0.wireOp",EDGE,"E4.18.0"),sQuery(id+"F0.wireOp",EDGE,"E4.19.0"),sQuery(id+"F0.wireOp",EDGE,"E4.20.0"),sQuery(id+"F0.wireOp",EDGE,"E4.21.0"),sQuery(id+"F0.wireOp",EDGE,"E4.22.0"),sQuery(id+"F0.wireOp",EDGE,"E4.23.0"),sQuery(id+"F0.wireOp",EDGE,"E4.24.0"),sQuery(id+"F0.wireOp",EDGE,"E4.25.0"),sQuery(id+"F0.wireOp",EDGE,"E4.26.0"),sQuery(id+"F0.wireOp",EDGE,"E4.27.0"),sQuery(id+"F0.wireOp",EDGE,"E4.28.0"),sQuery(id+"F0.wireOp",EDGE,"E4.29.0"),sQuery(id+"F0.wireOp",EDGE,"E4.31.0"),sQuery(id+"F0.wireOp",EDGE,"E4.32.0"),sQuery(id+"F0.wireOp",EDGE,"E4.33.0"),sQuery(id+"F0.wireOp",EDGE,"E4.34.0"),sQuery(id+"F0.wireOp",EDGE,"E4.35.0"),sQuery(id+"F0.wireOp",EDGE,"E4.36.0"),sQuery(id+"F0.wireOp",EDGE,"E4.37.0"),sQuery(id+"F0.wireOp",EDGE,"E4.38.0"),sQuery(id+"F0.wireOp",EDGE,"E4.39.0"),sQuery(id+"F0.wireOp",EDGE,"E4.40.0"),sQuery(id+"F0.wireOp",EDGE,"E4.41.0"),sQuery(id+"F0.wireOp",EDGE,"E4.42.0"),sQuery(id+"F0.wireOp",EDGE,"E4.43.0"),sQuery(id+"F0.wireOp",EDGE,"E4.44.0"),sQuery(id+"F0.wireOp",EDGE,"E4.45.0"),sQuery(id+"F0.wireOp",EDGE,"E4.46.0"),sQuery(id+"F0.wireOp",EDGE,"E4.47.0"),sQuery(id+"F0.wireOp",EDGE,"E4.48.0"),sQuery(id+"F0.wireOp",EDGE,"E4.49.0"),sQuery(id+"F0.wireOp",EDGE,"E4.50.0"),sQuery(id+"F0.wireOp",EDGE,"E4.51.0"),sQuery(id+"F0.wireOp",EDGE,"E4.52.0"),sQuery(id+"F0.wireOp",EDGE,"E4.53.0"),sQuery(id+"F0.wireOp",EDGE,"E4.54.0"),sQuery(id+"F0.wireOp",EDGE,"E4.55.0"),sQuery(id+"F0.wireOp",EDGE,"E4.56.0"),sQuery(id+"F0.wireOp",EDGE,"E4.57.0"),sQuery(id+"F0.wireOp",EDGE,"E4.58.0"),sQuery(id+"F0.wireOp",EDGE,"E4.59.0"),subQ3,sQuery(id+"F0.wireOp",EDGE,"E9"),subQ2,subQ1,sQuery(id+"F0.wireOp",EDGE,"E15.MirrorCS"),sQuery(id+"F0.wireOp",EDGE,"E16.MirrorCS"),sQuery(id+"F0.wireOp",EDGE,"E17.MirrorCS"),subQ0,sQuery(id+"F0.wireOp",EDGE,"E21.MirrorCS")])],"isStart":false}),makeQuery(id+"F4.opExtrude","SWEPT_FACE",FACE,{"disambiguationData":[OSD([subQ1])]})]}),makeQuery(id+"F4.opExtrude","CAP_FACE",FACE,{"disambiguationData":[OSD([subQ3,subQ2,subQ1,subQ0])],"isStart":false})],"blendedInto":[makeQuery(id+"F4.opExtrude","CAP_FACE",FACE,{"disambiguationData":[OSD([subQ3,subQ2,subQ1,subQ0])],"isStart":false})]});}
            var Q3;
            Q3=makeQuery(id+"F4.opExtrude","CAP_EDGE",EDGE,{"disambiguationData":[OSD([sQuery(id+"F0.wireOp",EDGE,"E19")])],"isStart":false});
            var Q4;
            Q4=makeQuery(id+"F4.opExtrude","CAP_EDGE",EDGE,{"disambiguationData":[OSD([sQuery(id+"F0.wireOp",EDGE,"E8")])],"isStart":false});
            var Q5;
            Q5=makeQuery(id+"F4.opExtrude","CAP_EDGE",EDGE,{"disambiguationData":[OSD([sQuery(id+"F0.wireOp",EDGE,"E15.MirrorCS")])],"isStart":false});
            var Q6;
            Q6=makeQuery(id+"F4.opExtrude","CAP_EDGE",EDGE,{"disambiguationData":[OSD([sQuery(id+"F0.wireOp",EDGE,"E17.MirrorCS")])],"isStart":false});
            var Q7;
            Q7=makeQuery(id+"F4.opExtrude","CAP_EDGE",EDGE,{"disambiguationData":[OSD([sQuery(id+"F0.wireOp",EDGE,"E21.MirrorCS")])],"isStart":false});
            var Q8;
            Q8=makeQuery(id+"F4.opExtrude","CAP_EDGE",EDGE,{"disambiguationData":[OSD([sQuery(id+"F0.wireOp",EDGE,"E16.MirrorCS")])],"isStart":false});
            var Q9;
            {var subQ0=sQuery(id+"F0.wireOp",EDGE,"E21.MirrorCS");var subQ1=sQuery(id+"F0.wireOp",EDGE,"E17.MirrorCS");var subQ2=sQuery(id+"F0.wireOp",EDGE,"E16.MirrorCS");var subQ3=sQuery(id+"F0.wireOp",EDGE,"E15.MirrorCS");var subQ4=sQuery(id+"F0.wireOp",EDGE,"E12");Q9=makeQuery(id+"F6.opFillet","BLEND_EDGE",EDGE,{"blendedFrom":[makeQuery(id+"F4.boolean.opBoolean","INTERSECT",EDGE,{"derivedFrom":[makeQuery(id+"F1.opExtrude","CAP_FACE",FACE,{"disambiguationData":[OSD([sQuery(id+"F0.wireOp",EDGE,"E1"),sQuery(id+"F0.wireOp",EDGE,"E2"),sQuery(id+"F0.wireOp",EDGE,"E4.1.0"),sQuery(id+"F0.wireOp",EDGE,"E4.2.0"),sQuery(id+"F0.wireOp",EDGE,"E4.3.0"),sQuery(id+"F0.wireOp",EDGE,"E4.4.0"),sQuery(id+"F0.wireOp",EDGE,"E4.5.0"),sQuery(id+"F0.wireOp",EDGE,"E4.6.0"),sQuery(id+"F0.wireOp",EDGE,"E4.7.0"),sQuery(id+"F0.wireOp",EDGE,"E4.8.0"),sQuery(id+"F0.wireOp",EDGE,"E4.9.0"),sQuery(id+"F0.wireOp",EDGE,"E4.10.0"),sQuery(id+"F0.wireOp",EDGE,"E4.11.0"),sQuery(id+"F0.wireOp",EDGE,"E4.12.0"),sQuery(id+"F0.wireOp",EDGE,"E4.13.0"),sQuery(id+"F0.wireOp",EDGE,"E4.14.0"),sQuery(id+"F0.wireOp",EDGE,"E4.15.0"),sQuery(id+"F0.wireOp",EDGE,"E4.16.0"),sQuery(id+"F0.wireOp",EDGE,"E4.17.0"),sQuery(id+"F0.wireOp",EDGE,"E4.18.0"),sQuery(id+"F0.wireOp",EDGE,"E4.19.0"),sQuery(id+"F0.wireOp",EDGE,"E4.20.0"),sQuery(id+"F0.wireOp",EDGE,"E4.21.0"),sQuery(id+"F0.wireOp",EDGE,"E4.22.0"),sQuery(id+"F0.wireOp",EDGE,"E4.23.0"),sQuery(id+"F0.wireOp",EDGE,"E4.24.0"),sQuery(id+"F0.wireOp",EDGE,"E4.25.0"),sQuery(id+"F0.wireOp",EDGE,"E4.26.0"),sQuery(id+"F0.wireOp",EDGE,"E4.27.0"),sQuery(id+"F0.wireOp",EDGE,"E4.28.0"),sQuery(id+"F0.wireOp",EDGE,"E4.29.0"),sQuery(id+"F0.wireOp",EDGE,"E4.31.0"),sQuery(id+"F0.wireOp",EDGE,"E4.32.0"),sQuery(id+"F0.wireOp",EDGE,"E4.33.0"),sQuery(id+"F0.wireOp",EDGE,"E4.34.0"),sQuery(id+"F0.wireOp",EDGE,"E4.35.0"),sQuery(id+"F0.wireOp",EDGE,"E4.36.0"),sQuery(id+"F0.wireOp",EDGE,"E4.37.0"),sQuery(id+"F0.wireOp",EDGE,"E4.38.0"),sQuery(id+"F0.wireOp",EDGE,"E4.39.0"),sQuery(id+"F0.wireOp",EDGE,"E4.40.0"),sQuery(id+"F0.wireOp",EDGE,"E4.41.0"),sQuery(id+"F0.wireOp",EDGE,"E4.42.0"),sQuery(id+"F0.wireOp",EDGE,"E4.43.0"),sQuery(id+"F0.wireOp",EDGE,"E4.44.0"),sQuery(id+"F0.wireOp",EDGE,"E4.45.0"),sQuery(id+"F0.wireOp",EDGE,"E4.46.0"),sQuery(id+"F0.wireOp",EDGE,"E4.47.0"),sQuery(id+"F0.wireOp",EDGE,"E4.48.0"),sQuery(id+"F0.wireOp",EDGE,"E4.49.0"),sQuery(id+"F0.wireOp",EDGE,"E4.50.0"),sQuery(id+"F0.wireOp",EDGE,"E4.51.0"),sQuery(id+"F0.wireOp",EDGE,"E4.52.0"),sQuery(id+"F0.wireOp",EDGE,"E4.53.0"),sQuery(id+"F0.wireOp",EDGE,"E4.54.0"),sQuery(id+"F0.wireOp",EDGE,"E4.55.0"),sQuery(id+"F0.wireOp",EDGE,"E4.56.0"),sQuery(id+"F0.wireOp",EDGE,"E4.57.0"),sQuery(id+"F0.wireOp",EDGE,"E4.58.0"),sQuery(id+"F0.wireOp",EDGE,"E4.59.0"),sQuery(id+"F0.wireOp",EDGE,"E8"),sQuery(id+"F0.wireOp",EDGE,"E9"),subQ4,sQuery(id+"F0.wireOp",EDGE,"E14"),subQ3,subQ2,subQ1,sQuery(id+"F0.wireOp",EDGE,"E19"),subQ0])],"isStart":false}),makeQuery(id+"F4.opExtrude","SWEPT_FACE",FACE,{"disambiguationData":[OSD([subQ2])]})]}),makeQuery(id+"F4.opExtrude","CAP_FACE",FACE,{"disambiguationData":[OSD([subQ4,subQ3,subQ2,subQ1,subQ0])],"isStart":false})],"blendedInto":[makeQuery(id+"F4.opExtrude","CAP_FACE",FACE,{"disambiguationData":[OSD([subQ4,subQ3,subQ2,subQ1,subQ0])],"isStart":false})]});}
            var Q10;
            {var subQ0=sQuery(id+"F0.wireOp",EDGE,"E21.MirrorCS");var subQ1=sQuery(id+"F0.wireOp",EDGE,"E17.MirrorCS");var subQ2=sQuery(id+"F0.wireOp",EDGE,"E16.MirrorCS");var subQ3=sQuery(id+"F0.wireOp",EDGE,"E15.MirrorCS");var subQ4=sQuery(id+"F0.wireOp",EDGE,"E12");Q10=makeQuery(id+"F7.opFillet","BLEND_EDGE",EDGE,{"blendedFrom":[makeQuery(id+"F4.boolean.opBoolean","INTERSECT",EDGE,{"derivedFrom":[makeQuery(id+"F1.opExtrude","CAP_FACE",FACE,{"disambiguationData":[OSD([sQuery(id+"F0.wireOp",EDGE,"E1"),sQuery(id+"F0.wireOp",EDGE,"E2"),sQuery(id+"F0.wireOp",EDGE,"E4.1.0"),sQuery(id+"F0.wireOp",EDGE,"E4.2.0"),sQuery(id+"F0.wireOp",EDGE,"E4.3.0"),sQuery(id+"F0.wireOp",EDGE,"E4.4.0"),sQuery(id+"F0.wireOp",EDGE,"E4.5.0"),sQuery(id+"F0.wireOp",EDGE,"E4.6.0"),sQuery(id+"F0.wireOp",EDGE,"E4.7.0"),sQuery(id+"F0.wireOp",EDGE,"E4.8.0"),sQuery(id+"F0.wireOp",EDGE,"E4.9.0"),sQuery(id+"F0.wireOp",EDGE,"E4.10.0"),sQuery(id+"F0.wireOp",EDGE,"E4.11.0"),sQuery(id+"F0.wireOp",EDGE,"E4.12.0"),sQuery(id+"F0.wireOp",EDGE,"E4.13.0"),sQuery(id+"F0.wireOp",EDGE,"E4.14.0"),sQuery(id+"F0.wireOp",EDGE,"E4.15.0"),sQuery(id+"F0.wireOp",EDGE,"E4.16.0"),sQuery(id+"F0.wireOp",EDGE,"E4.17.0"),sQuery(id+"F0.wireOp",EDGE,"E4.18.0"),sQuery(id+"F0.wireOp",EDGE,"E4.19.0"),sQuery(id+"F0.wireOp",EDGE,"E4.20.0"),sQuery(id+"F0.wireOp",EDGE,"E4.21.0"),sQuery(id+"F0.wireOp",EDGE,"E4.22.0"),sQuery(id+"F0.wireOp",EDGE,"E4.23.0"),sQuery(id+"F0.wireOp",EDGE,"E4.24.0"),sQuery(id+"F0.wireOp",EDGE,"E4.25.0"),sQuery(id+"F0.wireOp",EDGE,"E4.26.0"),sQuery(id+"F0.wireOp",EDGE,"E4.27.0"),sQuery(id+"F0.wireOp",EDGE,"E4.28.0"),sQuery(id+"F0.wireOp",EDGE,"E4.29.0"),sQuery(id+"F0.wireOp",EDGE,"E4.31.0"),sQuery(id+"F0.wireOp",EDGE,"E4.32.0"),sQuery(id+"F0.wireOp",EDGE,"E4.33.0"),sQuery(id+"F0.wireOp",EDGE,"E4.34.0"),sQuery(id+"F0.wireOp",EDGE,"E4.35.0"),sQuery(id+"F0.wireOp",EDGE,"E4.36.0"),sQuery(id+"F0.wireOp",EDGE,"E4.37.0"),sQuery(id+"F0.wireOp",EDGE,"E4.38.0"),sQuery(id+"F0.wireOp",EDGE,"E4.39.0"),sQuery(id+"F0.wireOp",EDGE,"E4.40.0"),sQuery(id+"F0.wireOp",EDGE,"E4.41.0"),sQuery(id+"F0.wireOp",EDGE,"E4.42.0"),sQuery(id+"F0.wireOp",EDGE,"E4.43.0"),sQuery(id+"F0.wireOp",EDGE,"E4.44.0"),sQuery(id+"F0.wireOp",EDGE,"E4.45.0"),sQuery(id+"F0.wireOp",EDGE,"E4.46.0"),sQuery(id+"F0.wireOp",EDGE,"E4.47.0"),sQuery(id+"F0.wireOp",EDGE,"E4.48.0"),sQuery(id+"F0.wireOp",EDGE,"E4.49.0"),sQuery(id+"F0.wireOp",EDGE,"E4.50.0"),sQuery(id+"F0.wireOp",EDGE,"E4.51.0"),sQuery(id+"F0.wireOp",EDGE,"E4.52.0"),sQuery(id+"F0.wireOp",EDGE,"E4.53.0"),sQuery(id+"F0.wireOp",EDGE,"E4.54.0"),sQuery(id+"F0.wireOp",EDGE,"E4.55.0"),sQuery(id+"F0.wireOp",EDGE,"E4.56.0"),sQuery(id+"F0.wireOp",EDGE,"E4.57.0"),sQuery(id+"F0.wireOp",EDGE,"E4.58.0"),sQuery(id+"F0.wireOp",EDGE,"E4.59.0"),sQuery(id+"F0.wireOp",EDGE,"E8"),sQuery(id+"F0.wireOp",EDGE,"E9"),subQ4,sQuery(id+"F0.wireOp",EDGE,"E14"),subQ3,subQ2,subQ1,sQuery(id+"F0.wireOp",EDGE,"E19"),subQ0])],"isStart":false}),makeQuery(id+"F4.opExtrude","SWEPT_FACE",FACE,{"disambiguationData":[OSD([subQ4]),TDD([makeQuery(id+"F0.imprint","IMPRINT",EDGE,{"disambiguationData":[TD([[makeQuery(id+"F0.imprint","INTERSECT",VERTEX,{"derivedFrom":[subQ4,subQ3]}),-1.0]])],"derivedFrom":subQ4})])]})]}),makeQuery(id+"F4.opExtrude","CAP_FACE",FACE,{"disambiguationData":[OSD([subQ4,subQ3,subQ2,subQ1,subQ0])],"isStart":false})],"blendedInto":[makeQuery(id+"F4.opExtrude","CAP_FACE",FACE,{"disambiguationData":[OSD([subQ4,subQ3,subQ2,subQ1,subQ0])],"isStart":false})]});}
            fillet(context, id + "F8", {"entities" : qUnion([Q0, Q1, Q2, Q3, Q4, Q5, Q6, Q7, Q8, Q9, Q10]), "radius" : 2 * mm, "tangentPropagation" : true, "allowEdgeOverflow" : false});
        }
        {
            var Q0;
            Q0=makeQuery(id+"F1.opExtrude","CAP_EDGE",EDGE,{"disambiguationData":[OSD([sQuery(id+"F0.wireOp",EDGE,"E16.MirrorCS")])],"isStart":true});
            var Q1;
            Q1=makeQuery(id+"F1.opExtrude","CAP_EDGE",EDGE,{"disambiguationData":[OSD([sQuery(id+"F0.wireOp",EDGE,"E21.MirrorCS")])],"isStart":true});
            var Q2;
            {var subQ0=sQuery(id+"F0.wireOp",EDGE,"E17.MirrorCS");Q2=makeQuery(id+"F4.boolean.opBoolean","MERGE",EDGE,{"derivedFrom":[makeQuery(id+"F1.opExtrude","CAP_EDGE",EDGE,{"disambiguationData":[OSD([subQ0])],"isStart":true}),makeQuery(id+"F4.opExtrude","CAP_EDGE",EDGE,{"disambiguationData":[OSD([subQ0])],"isStart":true})]});}
            var Q3;
            Q3=makeQuery(id+"F1.opExtrude","CAP_EDGE",EDGE,{"disambiguationData":[OSD([sQuery(id+"F0.wireOp",EDGE,"E15.MirrorCS")])],"isStart":true});
            var Q4;
            Q4=makeQuery(id+"F1.opExtrude","CAP_EDGE",EDGE,{"disambiguationData":[OSD([sQuery(id+"F0.wireOp",EDGE,"E8")])],"isStart":true});
            var Q5;
            Q5=makeQuery(id+"F1.opExtrude","CAP_EDGE",EDGE,{"disambiguationData":[OSD([sQuery(id+"F0.wireOp",EDGE,"E14")])],"isStart":true});
            var Q6;
            Q6=makeQuery(id+"F1.opExtrude","CAP_EDGE",EDGE,{"disambiguationData":[OSD([sQuery(id+"F0.wireOp",EDGE,"E19")])],"isStart":true});
            var Q7;
            {var subQ0=sQuery(id+"F0.wireOp",EDGE,"E14");var subQ1=sQuery(id+"F0.wireOp",EDGE,"E12");Q7=makeQuery(id+"F2.opFillet","BLEND_EDGE",EDGE,{"blendedFrom":[makeQuery(id+"F1.opExtrude","SWEPT_EDGE",EDGE,{"disambiguationData":[OSD([subQ1,subQ0])]}),makeQuery(id+"F1.opExtrude","CAP_FACE",FACE,{"disambiguationData":[OSD([sQuery(id+"F0.wireOp",EDGE,"E1"),sQuery(id+"F0.wireOp",EDGE,"E2"),sQuery(id+"F0.wireOp",EDGE,"E4.1.0"),sQuery(id+"F0.wireOp",EDGE,"E4.2.0"),sQuery(id+"F0.wireOp",EDGE,"E4.3.0"),sQuery(id+"F0.wireOp",EDGE,"E4.4.0"),sQuery(id+"F0.wireOp",EDGE,"E4.5.0"),sQuery(id+"F0.wireOp",EDGE,"E4.6.0"),sQuery(id+"F0.wireOp",EDGE,"E4.7.0"),sQuery(id+"F0.wireOp",EDGE,"E4.8.0"),sQuery(id+"F0.wireOp",EDGE,"E4.9.0"),sQuery(id+"F0.wireOp",EDGE,"E4.10.0"),sQuery(id+"F0.wireOp",EDGE,"E4.11.0"),sQuery(id+"F0.wireOp",EDGE,"E4.12.0"),sQuery(id+"F0.wireOp",EDGE,"E4.13.0"),sQuery(id+"F0.wireOp",EDGE,"E4.14.0"),sQuery(id+"F0.wireOp",EDGE,"E4.15.0"),sQuery(id+"F0.wireOp",EDGE,"E4.16.0"),sQuery(id+"F0.wireOp",EDGE,"E4.17.0"),sQuery(id+"F0.wireOp",EDGE,"E4.18.0"),sQuery(id+"F0.wireOp",EDGE,"E4.19.0"),sQuery(id+"F0.wireOp",EDGE,"E4.20.0"),sQuery(id+"F0.wireOp",EDGE,"E4.21.0"),sQuery(id+"F0.wireOp",EDGE,"E4.22.0"),sQuery(id+"F0.wireOp",EDGE,"E4.23.0"),sQuery(id+"F0.wireOp",EDGE,"E4.24.0"),sQuery(id+"F0.wireOp",EDGE,"E4.25.0"),sQuery(id+"F0.wireOp",EDGE,"E4.26.0"),sQuery(id+"F0.wireOp",EDGE,"E4.27.0"),sQuery(id+"F0.wireOp",EDGE,"E4.28.0"),sQuery(id+"F0.wireOp",EDGE,"E4.29.0"),sQuery(id+"F0.wireOp",EDGE,"E4.31.0"),sQuery(id+"F0.wireOp",EDGE,"E4.32.0"),sQuery(id+"F0.wireOp",EDGE,"E4.33.0"),sQuery(id+"F0.wireOp",EDGE,"E4.34.0"),sQuery(id+"F0.wireOp",EDGE,"E4.35.0"),sQuery(id+"F0.wireOp",EDGE,"E4.36.0"),sQuery(id+"F0.wireOp",EDGE,"E4.37.0"),sQuery(id+"F0.wireOp",EDGE,"E4.38.0"),sQuery(id+"F0.wireOp",EDGE,"E4.39.0"),sQuery(id+"F0.wireOp",EDGE,"E4.40.0"),sQuery(id+"F0.wireOp",EDGE,"E4.41.0"),sQuery(id+"F0.wireOp",EDGE,"E4.42.0"),sQuery(id+"F0.wireOp",EDGE,"E4.43.0"),sQuery(id+"F0.wireOp",EDGE,"E4.44.0"),sQuery(id+"F0.wireOp",EDGE,"E4.45.0"),sQuery(id+"F0.wireOp",EDGE,"E4.46.0"),sQuery(id+"F0.wireOp",EDGE,"E4.47.0"),sQuery(id+"F0.wireOp",EDGE,"E4.48.0"),sQuery(id+"F0.wireOp",EDGE,"E4.49.0"),sQuery(id+"F0.wireOp",EDGE,"E4.50.0"),sQuery(id+"F0.wireOp",EDGE,"E4.51.0"),sQuery(id+"F0.wireOp",EDGE,"E4.52.0"),sQuery(id+"F0.wireOp",EDGE,"E4.53.0"),sQuery(id+"F0.wireOp",EDGE,"E4.54.0"),sQuery(id+"F0.wireOp",EDGE,"E4.55.0"),sQuery(id+"F0.wireOp",EDGE,"E4.56.0"),sQuery(id+"F0.wireOp",EDGE,"E4.57.0"),sQuery(id+"F0.wireOp",EDGE,"E4.58.0"),sQuery(id+"F0.wireOp",EDGE,"E4.59.0"),sQuery(id+"F0.wireOp",EDGE,"E8"),sQuery(id+"F0.wireOp",EDGE,"E9"),subQ1,subQ0,sQuery(id+"F0.wireOp",EDGE,"E15.MirrorCS"),sQuery(id+"F0.wireOp",EDGE,"E16.MirrorCS"),sQuery(id+"F0.wireOp",EDGE,"E17.MirrorCS"),sQuery(id+"F0.wireOp",EDGE,"E19"),sQuery(id+"F0.wireOp",EDGE,"E21.MirrorCS")])],"isStart":true})],"blendedInto":[makeQuery(id+"F1.opExtrude","CAP_FACE",FACE,{"disambiguationData":[OSD([sQuery(id+"F0.wireOp",EDGE,"E1"),sQuery(id+"F0.wireOp",EDGE,"E2"),sQuery(id+"F0.wireOp",EDGE,"E4.1.0"),sQuery(id+"F0.wireOp",EDGE,"E4.2.0"),sQuery(id+"F0.wireOp",EDGE,"E4.3.0"),sQuery(id+"F0.wireOp",EDGE,"E4.4.0"),sQuery(id+"F0.wireOp",EDGE,"E4.5.0"),sQuery(id+"F0.wireOp",EDGE,"E4.6.0"),sQuery(id+"F0.wireOp",EDGE,"E4.7.0"),sQuery(id+"F0.wireOp",EDGE,"E4.8.0"),sQuery(id+"F0.wireOp",EDGE,"E4.9.0"),sQuery(id+"F0.wireOp",EDGE,"E4.10.0"),sQuery(id+"F0.wireOp",EDGE,"E4.11.0"),sQuery(id+"F0.wireOp",EDGE,"E4.12.0"),sQuery(id+"F0.wireOp",EDGE,"E4.13.0"),sQuery(id+"F0.wireOp",EDGE,"E4.14.0"),sQuery(id+"F0.wireOp",EDGE,"E4.15.0"),sQuery(id+"F0.wireOp",EDGE,"E4.16.0"),sQuery(id+"F0.wireOp",EDGE,"E4.17.0"),sQuery(id+"F0.wireOp",EDGE,"E4.18.0"),sQuery(id+"F0.wireOp",EDGE,"E4.19.0"),sQuery(id+"F0.wireOp",EDGE,"E4.20.0"),sQuery(id+"F0.wireOp",EDGE,"E4.21.0"),sQuery(id+"F0.wireOp",EDGE,"E4.22.0"),sQuery(id+"F0.wireOp",EDGE,"E4.23.0"),sQuery(id+"F0.wireOp",EDGE,"E4.24.0"),sQuery(id+"F0.wireOp",EDGE,"E4.25.0"),sQuery(id+"F0.wireOp",EDGE,"E4.26.0"),sQuery(id+"F0.wireOp",EDGE,"E4.27.0"),sQuery(id+"F0.wireOp",EDGE,"E4.28.0"),sQuery(id+"F0.wireOp",EDGE,"E4.29.0"),sQuery(id+"F0.wireOp",EDGE,"E4.31.0"),sQuery(id+"F0.wireOp",EDGE,"E4.32.0"),sQuery(id+"F0.wireOp",EDGE,"E4.33.0"),sQuery(id+"F0.wireOp",EDGE,"E4.34.0"),sQuery(id+"F0.wireOp",EDGE,"E4.35.0"),sQuery(id+"F0.wireOp",EDGE,"E4.36.0"),sQuery(id+"F0.wireOp",EDGE,"E4.37.0"),sQuery(id+"F0.wireOp",EDGE,"E4.38.0"),sQuery(id+"F0.wireOp",EDGE,"E4.39.0"),sQuery(id+"F0.wireOp",EDGE,"E4.40.0"),sQuery(id+"F0.wireOp",EDGE,"E4.41.0"),sQuery(id+"F0.wireOp",EDGE,"E4.42.0"),sQuery(id+"F0.wireOp",EDGE,"E4.43.0"),sQuery(id+"F0.wireOp",EDGE,"E4.44.0"),sQuery(id+"F0.wireOp",EDGE,"E4.45.0"),sQuery(id+"F0.wireOp",EDGE,"E4.46.0"),sQuery(id+"F0.wireOp",EDGE,"E4.47.0"),sQuery(id+"F0.wireOp",EDGE,"E4.48.0"),sQuery(id+"F0.wireOp",EDGE,"E4.49.0"),sQuery(id+"F0.wireOp",EDGE,"E4.50.0"),sQuery(id+"F0.wireOp",EDGE,"E4.51.0"),sQuery(id+"F0.wireOp",EDGE,"E4.52.0"),sQuery(id+"F0.wireOp",EDGE,"E4.53.0"),sQuery(id+"F0.wireOp",EDGE,"E4.54.0"),sQuery(id+"F0.wireOp",EDGE,"E4.55.0"),sQuery(id+"F0.wireOp",EDGE,"E4.56.0"),sQuery(id+"F0.wireOp",EDGE,"E4.57.0"),sQuery(id+"F0.wireOp",EDGE,"E4.58.0"),sQuery(id+"F0.wireOp",EDGE,"E4.59.0"),sQuery(id+"F0.wireOp",EDGE,"E8"),sQuery(id+"F0.wireOp",EDGE,"E9"),subQ1,subQ0,sQuery(id+"F0.wireOp",EDGE,"E15.MirrorCS"),sQuery(id+"F0.wireOp",EDGE,"E16.MirrorCS"),sQuery(id+"F0.wireOp",EDGE,"E17.MirrorCS"),sQuery(id+"F0.wireOp",EDGE,"E19"),sQuery(id+"F0.wireOp",EDGE,"E21.MirrorCS")])],"isStart":true})]});}
            var Q8;
            Q8=makeQuery(id+"F1.opExtrude","CAP_EDGE",EDGE,{"disambiguationData":[OSD([sQuery(id+"F0.wireOp",EDGE,"E12")])],"isStart":true});
            var Q9;
            {var subQ0=sQuery(id+"F0.wireOp",EDGE,"E16.MirrorCS");var subQ1=sQuery(id+"F0.wireOp",EDGE,"E12");Q9=makeQuery(id+"F2.opFillet","BLEND_EDGE",EDGE,{"blendedFrom":[makeQuery(id+"F1.opExtrude","SWEPT_EDGE",EDGE,{"disambiguationData":[OSD([subQ1,subQ0])]}),makeQuery(id+"F1.opExtrude","CAP_FACE",FACE,{"disambiguationData":[OSD([sQuery(id+"F0.wireOp",EDGE,"E1"),sQuery(id+"F0.wireOp",EDGE,"E2"),sQuery(id+"F0.wireOp",EDGE,"E4.1.0"),sQuery(id+"F0.wireOp",EDGE,"E4.2.0"),sQuery(id+"F0.wireOp",EDGE,"E4.3.0"),sQuery(id+"F0.wireOp",EDGE,"E4.4.0"),sQuery(id+"F0.wireOp",EDGE,"E4.5.0"),sQuery(id+"F0.wireOp",EDGE,"E4.6.0"),sQuery(id+"F0.wireOp",EDGE,"E4.7.0"),sQuery(id+"F0.wireOp",EDGE,"E4.8.0"),sQuery(id+"F0.wireOp",EDGE,"E4.9.0"),sQuery(id+"F0.wireOp",EDGE,"E4.10.0"),sQuery(id+"F0.wireOp",EDGE,"E4.11.0"),sQuery(id+"F0.wireOp",EDGE,"E4.12.0"),sQuery(id+"F0.wireOp",EDGE,"E4.13.0"),sQuery(id+"F0.wireOp",EDGE,"E4.14.0"),sQuery(id+"F0.wireOp",EDGE,"E4.15.0"),sQuery(id+"F0.wireOp",EDGE,"E4.16.0"),sQuery(id+"F0.wireOp",EDGE,"E4.17.0"),sQuery(id+"F0.wireOp",EDGE,"E4.18.0"),sQuery(id+"F0.wireOp",EDGE,"E4.19.0"),sQuery(id+"F0.wireOp",EDGE,"E4.20.0"),sQuery(id+"F0.wireOp",EDGE,"E4.21.0"),sQuery(id+"F0.wireOp",EDGE,"E4.22.0"),sQuery(id+"F0.wireOp",EDGE,"E4.23.0"),sQuery(id+"F0.wireOp",EDGE,"E4.24.0"),sQuery(id+"F0.wireOp",EDGE,"E4.25.0"),sQuery(id+"F0.wireOp",EDGE,"E4.26.0"),sQuery(id+"F0.wireOp",EDGE,"E4.27.0"),sQuery(id+"F0.wireOp",EDGE,"E4.28.0"),sQuery(id+"F0.wireOp",EDGE,"E4.29.0"),sQuery(id+"F0.wireOp",EDGE,"E4.31.0"),sQuery(id+"F0.wireOp",EDGE,"E4.32.0"),sQuery(id+"F0.wireOp",EDGE,"E4.33.0"),sQuery(id+"F0.wireOp",EDGE,"E4.34.0"),sQuery(id+"F0.wireOp",EDGE,"E4.35.0"),sQuery(id+"F0.wireOp",EDGE,"E4.36.0"),sQuery(id+"F0.wireOp",EDGE,"E4.37.0"),sQuery(id+"F0.wireOp",EDGE,"E4.38.0"),sQuery(id+"F0.wireOp",EDGE,"E4.39.0"),sQuery(id+"F0.wireOp",EDGE,"E4.40.0"),sQuery(id+"F0.wireOp",EDGE,"E4.41.0"),sQuery(id+"F0.wireOp",EDGE,"E4.42.0"),sQuery(id+"F0.wireOp",EDGE,"E4.43.0"),sQuery(id+"F0.wireOp",EDGE,"E4.44.0"),sQuery(id+"F0.wireOp",EDGE,"E4.45.0"),sQuery(id+"F0.wireOp",EDGE,"E4.46.0"),sQuery(id+"F0.wireOp",EDGE,"E4.47.0"),sQuery(id+"F0.wireOp",EDGE,"E4.48.0"),sQuery(id+"F0.wireOp",EDGE,"E4.49.0"),sQuery(id+"F0.wireOp",EDGE,"E4.50.0"),sQuery(id+"F0.wireOp",EDGE,"E4.51.0"),sQuery(id+"F0.wireOp",EDGE,"E4.52.0"),sQuery(id+"F0.wireOp",EDGE,"E4.53.0"),sQuery(id+"F0.wireOp",EDGE,"E4.54.0"),sQuery(id+"F0.wireOp",EDGE,"E4.55.0"),sQuery(id+"F0.wireOp",EDGE,"E4.56.0"),sQuery(id+"F0.wireOp",EDGE,"E4.57.0"),sQuery(id+"F0.wireOp",EDGE,"E4.58.0"),sQuery(id+"F0.wireOp",EDGE,"E4.59.0"),sQuery(id+"F0.wireOp",EDGE,"E8"),sQuery(id+"F0.wireOp",EDGE,"E9"),subQ1,sQuery(id+"F0.wireOp",EDGE,"E14"),sQuery(id+"F0.wireOp",EDGE,"E15.MirrorCS"),subQ0,sQuery(id+"F0.wireOp",EDGE,"E17.MirrorCS"),sQuery(id+"F0.wireOp",EDGE,"E19"),sQuery(id+"F0.wireOp",EDGE,"E21.MirrorCS")])],"isStart":true})],"blendedInto":[makeQuery(id+"F1.opExtrude","CAP_FACE",FACE,{"disambiguationData":[OSD([sQuery(id+"F0.wireOp",EDGE,"E1"),sQuery(id+"F0.wireOp",EDGE,"E2"),sQuery(id+"F0.wireOp",EDGE,"E4.1.0"),sQuery(id+"F0.wireOp",EDGE,"E4.2.0"),sQuery(id+"F0.wireOp",EDGE,"E4.3.0"),sQuery(id+"F0.wireOp",EDGE,"E4.4.0"),sQuery(id+"F0.wireOp",EDGE,"E4.5.0"),sQuery(id+"F0.wireOp",EDGE,"E4.6.0"),sQuery(id+"F0.wireOp",EDGE,"E4.7.0"),sQuery(id+"F0.wireOp",EDGE,"E4.8.0"),sQuery(id+"F0.wireOp",EDGE,"E4.9.0"),sQuery(id+"F0.wireOp",EDGE,"E4.10.0"),sQuery(id+"F0.wireOp",EDGE,"E4.11.0"),sQuery(id+"F0.wireOp",EDGE,"E4.12.0"),sQuery(id+"F0.wireOp",EDGE,"E4.13.0"),sQuery(id+"F0.wireOp",EDGE,"E4.14.0"),sQuery(id+"F0.wireOp",EDGE,"E4.15.0"),sQuery(id+"F0.wireOp",EDGE,"E4.16.0"),sQuery(id+"F0.wireOp",EDGE,"E4.17.0"),sQuery(id+"F0.wireOp",EDGE,"E4.18.0"),sQuery(id+"F0.wireOp",EDGE,"E4.19.0"),sQuery(id+"F0.wireOp",EDGE,"E4.20.0"),sQuery(id+"F0.wireOp",EDGE,"E4.21.0"),sQuery(id+"F0.wireOp",EDGE,"E4.22.0"),sQuery(id+"F0.wireOp",EDGE,"E4.23.0"),sQuery(id+"F0.wireOp",EDGE,"E4.24.0"),sQuery(id+"F0.wireOp",EDGE,"E4.25.0"),sQuery(id+"F0.wireOp",EDGE,"E4.26.0"),sQuery(id+"F0.wireOp",EDGE,"E4.27.0"),sQuery(id+"F0.wireOp",EDGE,"E4.28.0"),sQuery(id+"F0.wireOp",EDGE,"E4.29.0"),sQuery(id+"F0.wireOp",EDGE,"E4.31.0"),sQuery(id+"F0.wireOp",EDGE,"E4.32.0"),sQuery(id+"F0.wireOp",EDGE,"E4.33.0"),sQuery(id+"F0.wireOp",EDGE,"E4.34.0"),sQuery(id+"F0.wireOp",EDGE,"E4.35.0"),sQuery(id+"F0.wireOp",EDGE,"E4.36.0"),sQuery(id+"F0.wireOp",EDGE,"E4.37.0"),sQuery(id+"F0.wireOp",EDGE,"E4.38.0"),sQuery(id+"F0.wireOp",EDGE,"E4.39.0"),sQuery(id+"F0.wireOp",EDGE,"E4.40.0"),sQuery(id+"F0.wireOp",EDGE,"E4.41.0"),sQuery(id+"F0.wireOp",EDGE,"E4.42.0"),sQuery(id+"F0.wireOp",EDGE,"E4.43.0"),sQuery(id+"F0.wireOp",EDGE,"E4.44.0"),sQuery(id+"F0.wireOp",EDGE,"E4.45.0"),sQuery(id+"F0.wireOp",EDGE,"E4.46.0"),sQuery(id+"F0.wireOp",EDGE,"E4.47.0"),sQuery(id+"F0.wireOp",EDGE,"E4.48.0"),sQuery(id+"F0.wireOp",EDGE,"E4.49.0"),sQuery(id+"F0.wireOp",EDGE,"E4.50.0"),sQuery(id+"F0.wireOp",EDGE,"E4.51.0"),sQuery(id+"F0.wireOp",EDGE,"E4.52.0"),sQuery(id+"F0.wireOp",EDGE,"E4.53.0"),sQuery(id+"F0.wireOp",EDGE,"E4.54.0"),sQuery(id+"F0.wireOp",EDGE,"E4.55.0"),sQuery(id+"F0.wireOp",EDGE,"E4.56.0"),sQuery(id+"F0.wireOp",EDGE,"E4.57.0"),sQuery(id+"F0.wireOp",EDGE,"E4.58.0"),sQuery(id+"F0.wireOp",EDGE,"E4.59.0"),sQuery(id+"F0.wireOp",EDGE,"E8"),sQuery(id+"F0.wireOp",EDGE,"E9"),subQ1,sQuery(id+"F0.wireOp",EDGE,"E14"),sQuery(id+"F0.wireOp",EDGE,"E15.MirrorCS"),subQ0,sQuery(id+"F0.wireOp",EDGE,"E17.MirrorCS"),sQuery(id+"F0.wireOp",EDGE,"E19"),sQuery(id+"F0.wireOp",EDGE,"E21.MirrorCS")])],"isStart":true})]});}
            fillet(context, id + "F9", {"entities" : qUnion([Q0, Q1, Q2, Q3, Q4, Q5, Q6, Q7, Q8, Q9]), "radius" : 2 * mm, "tangentPropagation" : true, "allowEdgeOverflow" : false});
        }
        {
            var Q0;
            Q0=makeQuery(id+"F1.opExtrude","CAP_EDGE",EDGE,{"disambiguationData":[OSD([sQuery(id+"F0.wireOp",EDGE,"E12")])],"isStart":false});
            fillet(context, id + "F10", {"entities" : qUnion([Q0]), "radius" : 2 * mm, "tangentPropagation" : true, "allowEdgeOverflow" : false});
        }
    });
